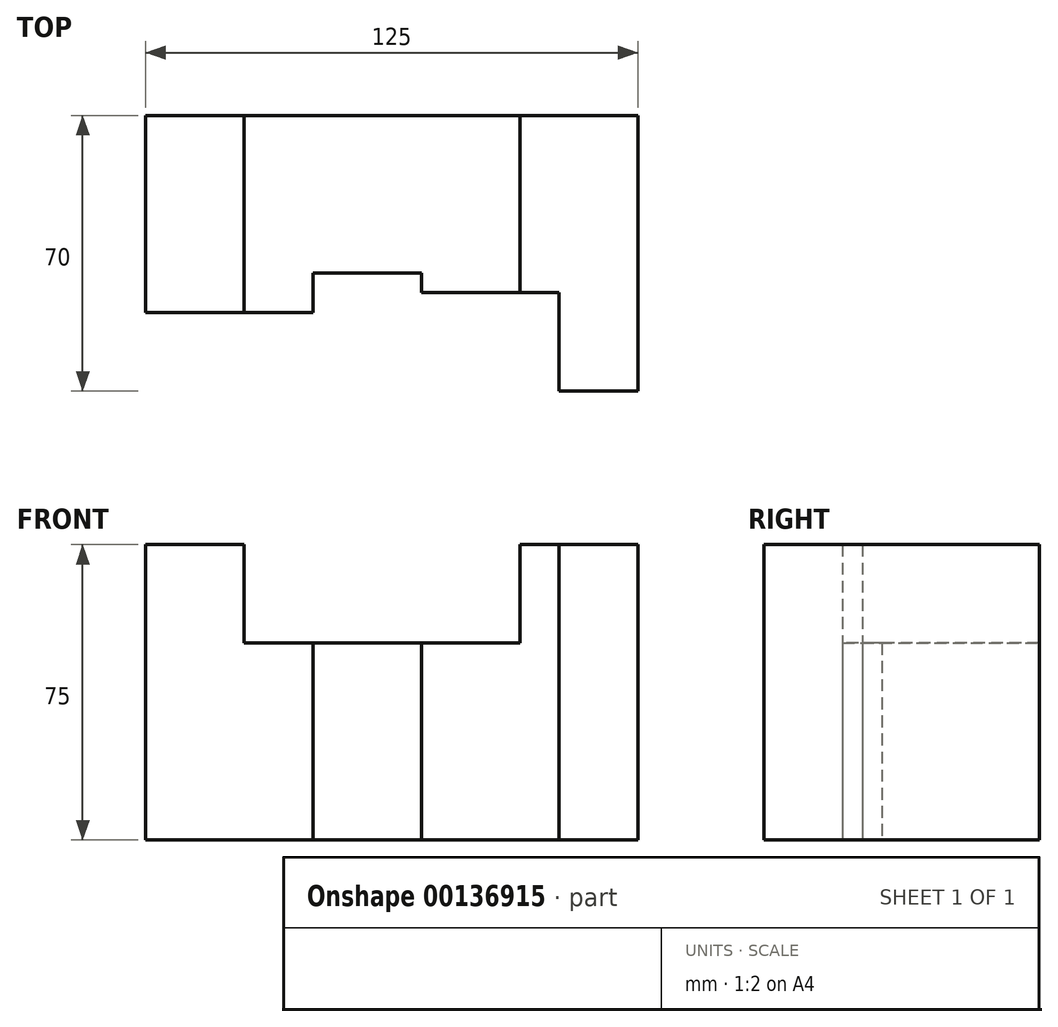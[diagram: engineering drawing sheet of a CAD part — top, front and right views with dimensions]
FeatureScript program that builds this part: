
annotation { "Feature Type Name" : "Feature", "Feature Type Description" : "" }
export const myFeature = defineFeature(function(context is Context, id is Id, definition is map)
    precondition{}
    {
        {
            var Q0;
            Q0=qCreatedBy(makeId("Top.planeOp"),FACE);
            var sketch = newSketch(context, id + "F0", { "sketchPlane" : qUnion([Q0])});
            skLineSegment(sketch, "E0.bottom", {"start": v(0, 0) * mm, "end": v(42.5, 0) * mm});
            skLineSegment(sketch, "E0.top", {"start": v(0, 50) * mm, "end": v(42.5, 50) * mm});
            skLineSegment(sketch, "E0.left", {"start": v(0, 0) * mm, "end": v(0, 50) * mm});
            skLineSegment(sketch, "E0.right", {"start": v(42.5, 0) * mm, "end": v(42.5, 10) * mm});
            skLineSegment(sketch, "E1", {"start": v(25, 50) * mm, "end": v(25, 0) * mm});
            skLineSegment(sketch, "E2.bottom", {"start": v(42.5, 50) * mm, "end": v(70, 50) * mm});
            skLineSegment(sketch, "E2.top", {"start": v(42.5, 10) * mm, "end": v(70, 10) * mm});
            skLineSegment(sketch, "E3.bottom", {"start": v(70, 50) * mm, "end": v(125, 50) * mm});
            skLineSegment(sketch, "E3.top", {"start": v(70, 5) * mm, "end": v(105, 5) * mm});
            skLineSegment(sketch, "E3.left", {"start": v(70, 10) * mm, "end": v(70, 5) * mm});
            skLineSegment(sketch, "E3.right", {"start": v(125, 50) * mm, "end": v(125, 5) * mm});
            skLineSegment(sketch, "E4.top", {"start": v(125, -20) * mm, "end": v(105, -20) * mm});
            skLineSegment(sketch, "E4.left", {"start": v(125, 5) * mm, "end": v(125, -20) * mm});
            skLineSegment(sketch, "E4.right", {"start": v(105, 5) * mm, "end": v(105, -20) * mm});
            skLineSegment(sketch, "E5", {"start": v(95, 5) * mm, "end": v(95, 50) * mm});
            skSolve(sketch);
        }
        {
            var Q0;
            {var subQ0=sQuery(id+"F0.wireOp",EDGE,"E0.left");Q0=makeQuery(id+"F0.imprint","IMPRINT",FACE,{"disambiguationData":[TD([[makeQuery(id+"F0.imprint","IMPRINT",EDGE,{"derivedFrom":subQ0}),-1.0]])]});}
            extrude(context, id + "F1", {"entities" : qUnion([Q0]), "depth" : 75 * mm});
        }
        {
            var Q0;
            {var subQ2=sQuery(id+"F0.wireOp",EDGE,"E0.right");Q0=makeQuery(id+"F0.imprint","IMPRINT",FACE,{"disambiguationData":[TD([[makeQuery(id+"F0.imprint","IMPRINT",EDGE,{"derivedFrom":subQ2}),1.0]])]});}
            extrude(context, id + "F2", {"entities" : qUnion([Q0]), "operationType" : NewBodyOperationType.ADD, "depth" : 50 * mm});
        }
        {
            var Q0;
            {var subQ0=sQuery(id+"F0.wireOp",EDGE,"E3.right");Q0=makeQuery(id+"F0.imprint","IMPRINT",FACE,{"disambiguationData":[TD([[makeQuery(id+"F0.imprint","IMPRINT",EDGE,{"derivedFrom":subQ0}),-1.0]])]});}
            extrude(context, id + "F3", {"entities" : qUnion([Q0]), "operationType" : NewBodyOperationType.ADD, "depth" : 75 * mm});
        }
    });
